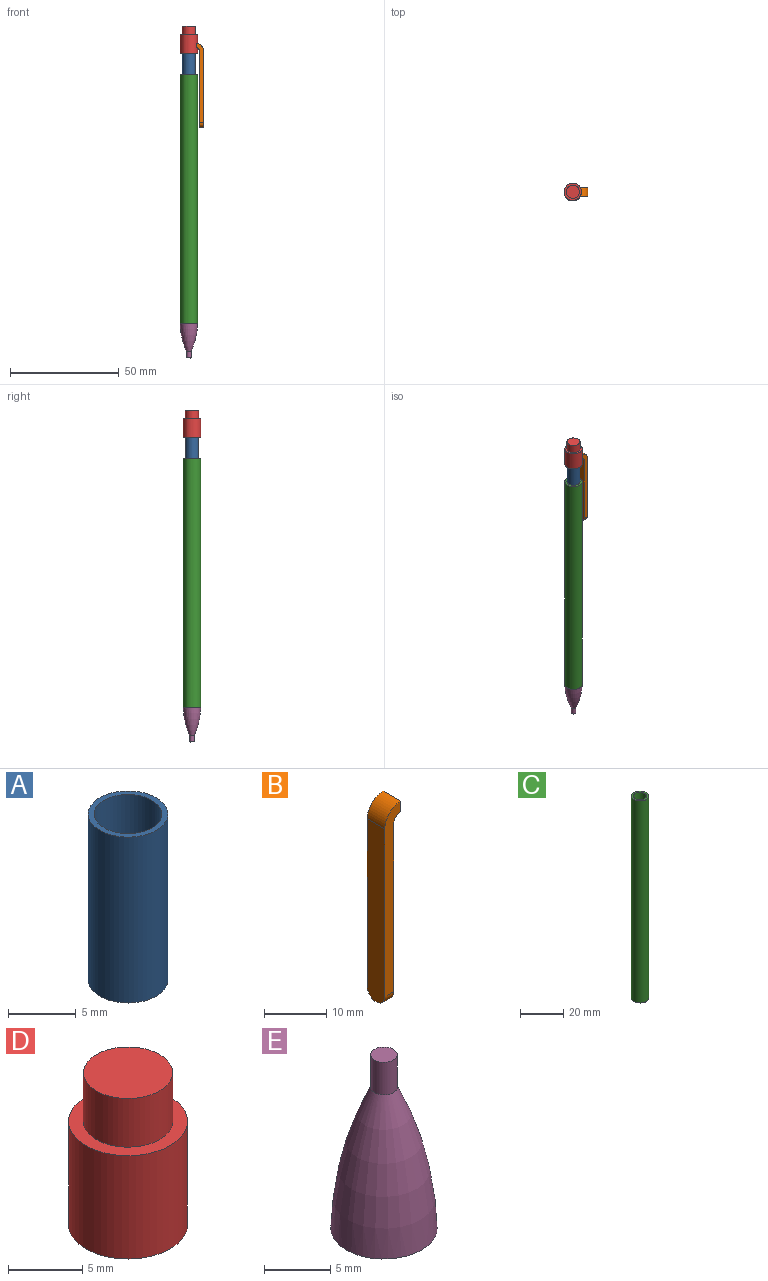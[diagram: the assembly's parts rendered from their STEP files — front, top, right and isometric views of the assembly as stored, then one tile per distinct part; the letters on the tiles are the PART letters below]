
ASSEMBLY  parts=5 mates=4
PART A: 4 faces, bbox 5.9x5.9x15 mm
  f0: cylinder r=2.5mm len=15mm, axis (0,0,-1), area 235.6mm2, adj f2,f3
  f1: cylinder r=2.95mm len=15mm, axis (0,0,-1), area 278mm2, adj f2,f3
  f2: plane 5.9x5.9mm, normal (0,0,1), area 7.7mm2, adj f0,f1
  f3: plane 5.9x5.9mm, normal (0,0,-1), area 7.7mm2, adj f0,f1
PART B: 9 faces, bbox 3.6x4x38.7 mm
  f0: cylinder r=3.65mm len=4mm, axis (0,1,0), area 22.8mm2, adj f1,f4,f5,f6
  f1: plane 35x4mm, normal (-1,0,0), area 138.2mm2, adj f0,f5,f6,f7,f8
  f2: plane 35x4mm, normal (1,0,0), area 138.2mm2, adj f3,f5,f6,f7,f8
  f3: cylinder r=1.65mm len=4mm, axis (0,1,0), area 10.2mm2, adj f2,f4,f5,f6
  f4: plane 4x2mm, normal (1,0,0), area 8mm2, adj f0,f3,f5,f6
  f5: plane 36.62x3.61mm, normal (0,-1,0), area 74.2mm2, adj f0,f1,f2,f3,f4,f7
  f6: plane 36.62x3.61mm, normal (0,1,0), area 74.2mm2, adj f0,f1,f2,f3,f4,f8
  f7: cylinder r=2.03mm len=2.03mm, axis (-1,0,0), area 6.3mm2, adj f1,f2,f5,f8
  f8: cylinder r=2.03mm len=2.03mm, axis (1,0,0), area 6.3mm2, adj f1,f2,f6,f7
PART C: 4 faces, bbox 8x8x114.3 mm
  f0: cylinder r=3mm len=114.3mm, axis (0,0,1), area 2154.5mm2, adj f2,f3
  f1: cylinder r=4mm len=114.3mm, axis (0,0,1), area 2872.7mm2, adj f2,f3
  f2: plane 8x8mm, normal (0,0,-1), area 22mm2, adj f0,f1
  f3: plane 8x8mm, normal (0,0,1), area 22mm2, adj f0,f1
PART D: 10 faces, bbox 8x8x12.5 mm
  f0: cylinder r=4mm len=8.5mm, axis (0,0,-1), area 205.2mm2, adj f1,f2,f5,f6,f7,f8
  f1: plane 8x8mm, normal (0,0,1), area 22mm2, adj f0,f3
  f2: plane 8x8mm, normal (0,0,-1), area 50.3mm2, adj f0
  f3: cylinder r=3mm len=6mm, axis (0,0,-1), area 75.4mm2, adj f1,f4
  f4: plane 6x6mm, normal (0,0,1), area 28.3mm2, adj f3
  f5: plane 4x0.7mm, normal (0,0,-1), area 2.1mm2, adj f0,f6,f8,f9
  f6: plane 2x0.16mm, normal (0,1,0), area 0.3mm2, adj f0,f5,f7,f9
  f7: plane 4x0.7mm, normal (0,0,1), area 2.1mm2, adj f0,f6,f8,f9
  f8: plane 2x0.17mm, normal (0,-1,0), area 0.3mm2, adj f0,f5,f7,f9
  f9: plane 4x2mm, normal (1,0,0), area 8mm2, adj f5,f6,f7,f8
PART E: 4 faces, bbox 8x8x16 mm
  f0: plane 8x8mm, normal (0,0,-1), area 50.3mm2, adj f3
  f1: plane 2x2mm, normal (0,0,1), area 3.1mm2, adj f2
  f2: cylinder r=1mm len=3mm, axis (0,0,-1), area 18.9mm2, adj f1,f3
  f3: revolved ~13x8mm, area 249.5mm2, adj f0,f2
PLACE A t=(-31.9,-6.47,11.46)mm
PLACE B rot(axis=(0,0,1),180deg) t=(-24.99,-8.48,27.31)mm
PLACE C t=(-31.9,-6.47,16.46)mm fixed
PLACE D t=(-31.9,-6.47,26.46)mm
PLACE E rot(axis=(1,0,0),180deg) t=(-31.9,-6.47,-97.84)mm
MATE fastened E.f2 <-> C.f0  axis (0,0,1) through (-31.9,-6.47,-97.84)mm
MATE slider A.f0 <-> C.f1  axis (0,0,-1) through (-31.9,-6.47,11.46)mm
MATE fastened D.f0 <-> A.f1  axis (0,0,-1) through (-31.9,-6.47,26.46)mm
MATE fastened B.f4 <-> D.f9  axis (-1,0,0) through (-28.6,-6.48,29.96)mm
